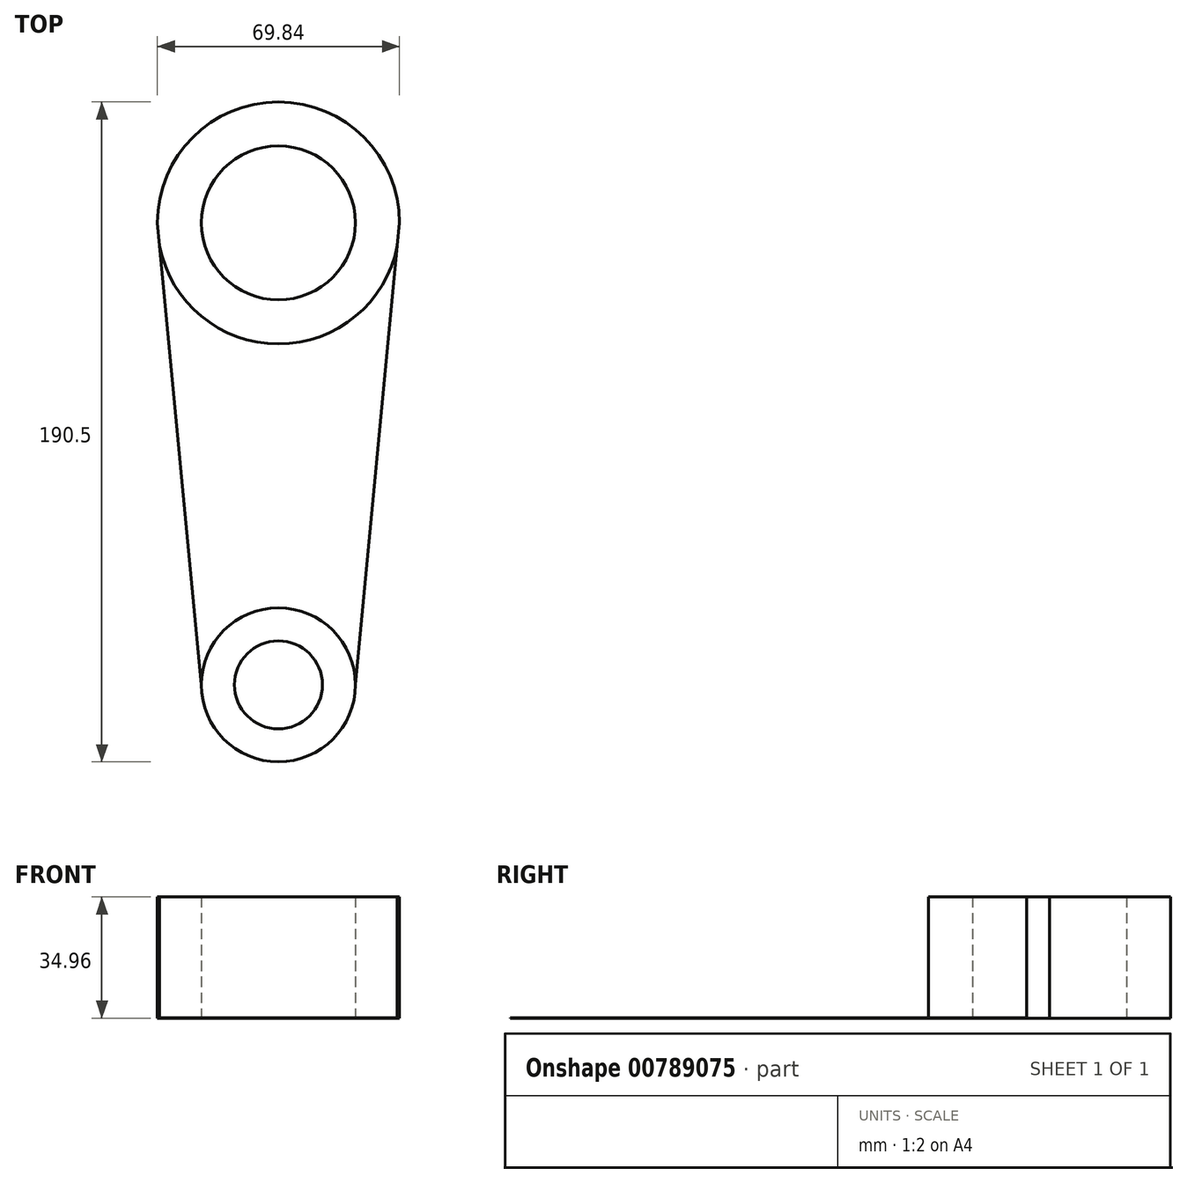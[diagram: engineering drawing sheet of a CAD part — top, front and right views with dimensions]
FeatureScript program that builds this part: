
annotation { "Feature Type Name" : "Feature", "Feature Type Description" : "" }
export const myFeature = defineFeature(function(context is Context, id is Id, definition is map)
    precondition{}
    {
        {
            var Q0;
            Q0=qCreatedBy(makeId("Top.planeOp"),FACE);
            var sketch = newSketch(context, id + "F0", { "sketchPlane" : qUnion([Q0])});
            skLineSegment(sketch, "E0", {"start": v(0, 0) * mm, "end": v(0, 133.35) * mm, "construction": true});
            skCircle(sketch, "E1", {"center": v(0, 133.35) * mm, "radius": 22.23 * mm});
            skCircle(sketch, "E2", {"center": v(0, 133.35) * mm, "radius": 34.93 * mm});
            skCircle(sketch, "E3", {"center": v(0, 0) * mm, "radius": 12.7 * mm});
            skCircle(sketch, "E4", {"center": v(0, 0) * mm, "radius": 22.23 * mm});
            skLineSegment(sketch, "E5", {"start": v(0, 133.35) * mm, "end": v(-34.93, 133.35) * mm, "construction": true});
            skLineSegment(sketch, "E6", {"start": v(0, 133.35) * mm, "end": v(34.93, 133.35) * mm, "construction": true});
            skLineSegment(sketch, "E7", {"start": v(0, 0) * mm, "end": v(22.23, 0) * mm, "construction": true});
            skLineSegment(sketch, "E8", {"start": v(0, 0) * mm, "end": v(-22.23, 0) * mm, "construction": true});
            skLineSegment(sketch, "E9", {"start": v(-22.22, 0) * mm, "end": v(-34.93, 133.35) * mm});
            skLineSegment(sketch, "E10", {"start": v(22.22, 0) * mm, "end": v(34.93, 133.35) * mm});
            skSolve(sketch);
        }
        {
            var Q0;
            Q0=makeQuery(id+"F0.imprint","IMPRINT",FACE,{"disambiguationData":[TD([[makeQuery(id+"F0.imprint","IMPRINT",EDGE,{"derivedFrom":sQuery(id+"F0.wireOp",EDGE,"E1")}),-1.0]])]});
            var Q1;
            Q1=makeQuery(id+"F0.imprint","IMPRINT",FACE,{"disambiguationData":[TD([[makeQuery(id+"F0.imprint","IMPRINT",EDGE,{"derivedFrom":sQuery(id+"F0.wireOp",EDGE,"E1")}),1.0]])]});
            var Q2;
            {var subQ0=sQuery(id+"F0.wireOp",EDGE,"E9");var subQ1=sQuery(id+"F0.wireOp",EDGE,"E2");var subQ2=makeQuery(id+"F0.imprint","INTERSECT",VERTEX,{"disambiguationData":[OD(1.0)],"derivedFrom":[subQ1,subQ0]});Q2=makeQuery(id+"F0.imprint","IMPRINT",FACE,{"disambiguationData":[TD([[makeQuery(id+"F0.imprint","IMPRINT",EDGE,{"disambiguationData":[TD([[subQ2,-1.0]])],"derivedFrom":subQ1}),-1.0]])]});}
            var Q3;
            Q3=makeQuery(id+"F0.imprint","IMPRINT",FACE,{"disambiguationData":[TD([[makeQuery(id+"F0.imprint","IMPRINT",EDGE,{"derivedFrom":sQuery(id+"F0.wireOp",EDGE,"E3")}),1.0]])]});
            var Q4;
            Q4=makeQuery(id+"F0.imprint","IMPRINT",FACE,{"disambiguationData":[TD([[makeQuery(id+"F0.imprint","IMPRINT",EDGE,{"derivedFrom":sQuery(id+"F0.wireOp",EDGE,"E3")}),-1.0]])]});
            extrude(context, id + "F1", {"entities" : qUnion([Q0, Q1, Q2, Q3, Q4]), "depth" : 7 / 203.2 * mm, "offsetDistance" : 25.4 * mm});
        }
        {
            var Q0;
            Q0=makeQuery(id+"F1.opExtrude","CAP_FACE",FACE,{"disambiguationData":[OSD([sQuery(id+"F0.wireOp",EDGE,"E2"),sQuery(id+"F0.wireOp",EDGE,"E4"),sQuery(id+"F0.wireOp",EDGE,"E9"),sQuery(id+"F0.wireOp",EDGE,"E10")])],"isStart":false});
            var sketch = newSketch(context, id + "F2", { "sketchPlane" : qUnion([Q0])});
            skCircle(sketch, "E11", {"center": v(0, 0) * mm, "radius": 12.7 * mm});
            skCircle(sketch, "E12", {"center": v(0, 0) * mm, "radius": 22.23 * mm});
            skLineSegment(sketch, "E13", {"start": v(0, 0) * mm, "end": v(0, 133.35) * mm, "construction": true});
            skCircle(sketch, "E14", {"center": v(0, 133.35) * mm, "radius": 22.23 * mm});
            skCircle(sketch, "E15", {"center": v(0, 133.35) * mm, "radius": 34.93 * mm});
            skSolve(sketch);
        }
        {
            var Q0;
            Q0=makeQuery(id+"F2.imprint","IMPRINT",FACE,{"disambiguationData":[TD([[makeQuery(id+"F2.imprint","IMPRINT",EDGE,{"derivedFrom":sQuery(id+"F2.wireOp",EDGE,"E14")}),-1.0]])]});
            extrude(context, id + "F3", {"entities" : qUnion([Q0]), "operationType" : NewBodyOperationType.ADD, "depth" : 34.92 * mm, "offsetDistance" : 25.4 * mm});
        }
        {
            var Q0;
            Q0=makeQuery(id+"F3.boolean.opBoolean","SPLIT",FACE,{"disambiguationData":[TD([makeQuery(id+"F3.opExtrude","SWEPT_FACE",FACE,{"disambiguationData":[OSD([sQuery(id+"F2.wireOp",EDGE,"E14")])]})])],"derivedFrom":makeQuery(id+"F1.opExtrude","CAP_FACE",FACE,{"disambiguationData":[OSD([sQuery(id+"F0.wireOp",EDGE,"E2"),sQuery(id+"F0.wireOp",EDGE,"E4"),sQuery(id+"F0.wireOp",EDGE,"E9"),sQuery(id+"F0.wireOp",EDGE,"E10")])],"isStart":false})});
            extrude(context, id + "F4", {"entities" : qUnion([Q0]), "operationType" : NewBodyOperationType.REMOVE, "oppositeDirection" : true, "depth" : 50.8 * mm, "offsetDistance" : 25.4 * mm});
        }
        {
            var Q0;
            {var subQ1=sQuery(id+"F0.wireOp",EDGE,"E9");var subQ2=sQuery(id+"F0.wireOp",EDGE,"E10");var subQ3=sQuery(id+"F0.wireOp",EDGE,"E4");Q0=makeQuery(id+"F3.boolean.opBoolean","SPLIT",FACE,{"disambiguationData":[TD([makeQuery(id+"F1.opExtrude","SWEPT_FACE",FACE,{"disambiguationData":[OSD([subQ3])]})])],"derivedFrom":makeQuery(id+"F1.opExtrude","CAP_FACE",FACE,{"disambiguationData":[OSD([sQuery(id+"F0.wireOp",EDGE,"E2"),subQ3,subQ1,subQ2])],"isStart":false})});}
            var sketch = newSketch(context, id + "F5", { "sketchPlane" : qUnion([Q0])});
            skCircle(sketch, "E16", {"center": v(0, 0) * mm, "radius": 12.7 * mm});
            skCircle(sketch, "E17", {"center": v(0, 0) * mm, "radius": 22.23 * mm});
            skSolve(sketch);
        }
        {
            var Q0;
            Q0=makeQuery(id+"F5.imprint","IMPRINT",FACE,{"disambiguationData":[TD([[makeQuery(id+"F5.imprint","IMPRINT",EDGE,{"derivedFrom":sQuery(id+"F5.wireOp",EDGE,"E16")}),-1.0]])]});
            var Q1;
            Q1=makeQuery(id+"F5.imprint","IMPRINT",FACE,{"disambiguationData":[TD([[makeQuery(id+"F5.imprint","IMPRINT",EDGE,{"derivedFrom":sQuery(id+"F5.wireOp",EDGE,"E16")}),1.0]])]});
            extrude(context, id + "F6", {"entities" : qUnion([Q0, Q1]), "operationType" : NewBodyOperationType.ADD, "depth" : 5 / 203.2 * mm, "offsetDistance" : 25.4 * mm});
        }
        {
            var Q0;
            Q0=makeQuery(id+"F6.opExtrude","CAP_FACE",FACE,{"disambiguationData":[OSD([sQuery(id+"F5.wireOp",EDGE,"E17")])],"isStart":false});
            var sketch = newSketch(context, id + "F7", { "sketchPlane" : qUnion([Q0])});
            skCircle(sketch, "E18", {"center": v(0, 0) * mm, "radius": 12.7 * mm});
            skSolve(sketch);
        }
        {
            var Q0;
            Q0 = qSketchRegion(id + "F7", true);
            extrude(context, id + "F8", {"entities" : qUnion([Q0]), "operationType" : NewBodyOperationType.REMOVE, "oppositeDirection" : true, "depth" : 38.1 * mm, "offsetDistance" : 25.4 * mm});
        }
    });
